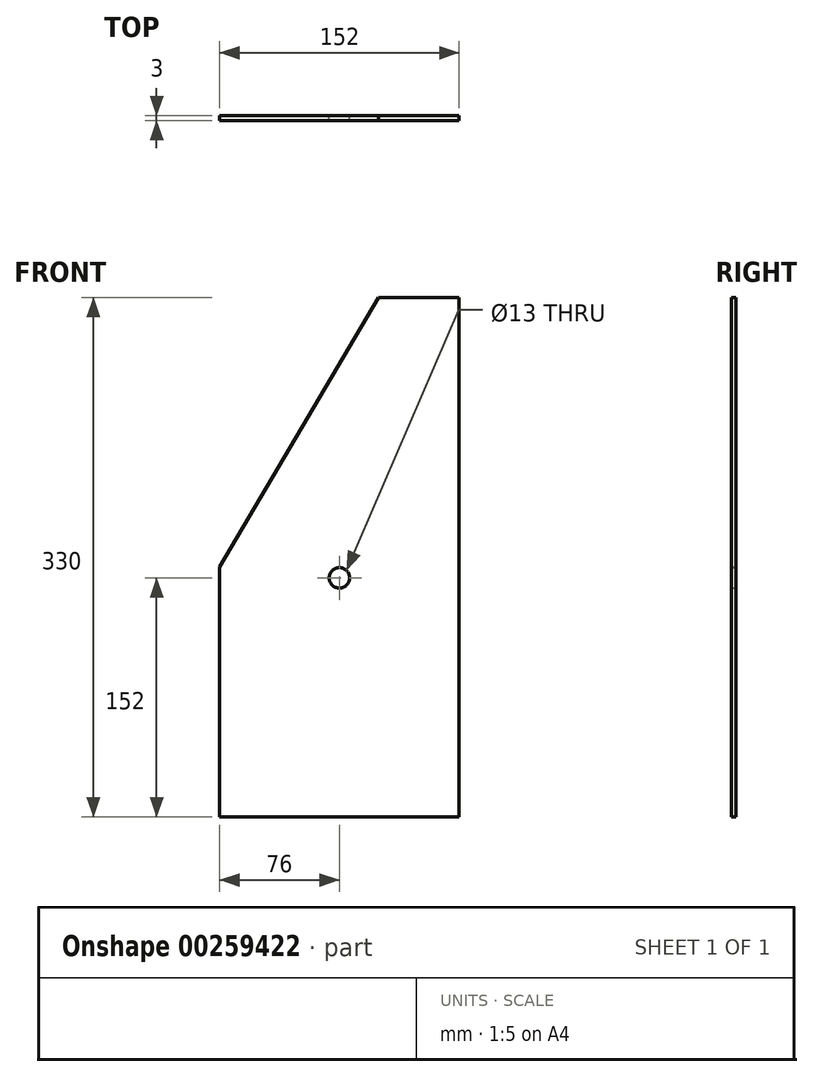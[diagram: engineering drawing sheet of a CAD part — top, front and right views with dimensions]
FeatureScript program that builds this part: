
annotation { "Feature Type Name" : "Feature", "Feature Type Description" : "" }
export const myFeature = defineFeature(function(context is Context, id is Id, definition is map)
    precondition{}
    {
        {
            var Q0;
            Q0=qCreatedBy(makeId("Front.planeOp"),FACE);
            var sketch = newSketch(context, id + "F0", { "sketchPlane" : qUnion([Q0])});
            skLineSegment(sketch, "E0", {"start": v(-76, -152) * mm, "end": v(76, -152) * mm});
            skLineSegment(sketch, "E1", {"start": v(76, -152) * mm, "end": v(76, 178) * mm});
            skLineSegment(sketch, "E2", {"start": v(76, 178) * mm, "end": v(25, 178) * mm});
            skLineSegment(sketch, "E3", {"start": v(25, 178) * mm, "end": v(-76, 7) * mm});
            skLineSegment(sketch, "E4", {"start": v(-76, 7) * mm, "end": v(-76, -152) * mm});
            skCircle(sketch, "E5", {"center": v(0, 0) * mm, "radius": 6.5 * mm});
            skSolve(sketch);
        }
        {
            var Q0;
            Q0=makeQuery(id+"F0.imprint","IMPRINT",FACE,{"disambiguationData":[TD([[makeQuery(id+"F0.imprint","IMPRINT",EDGE,{"derivedFrom":sQuery(id+"F0.wireOp",EDGE,"E0")}),1.0]])]});
            extrude(context, id + "F1", {"entities" : qUnion([Q0]), "depth" : 3 * mm});
        }
    });
